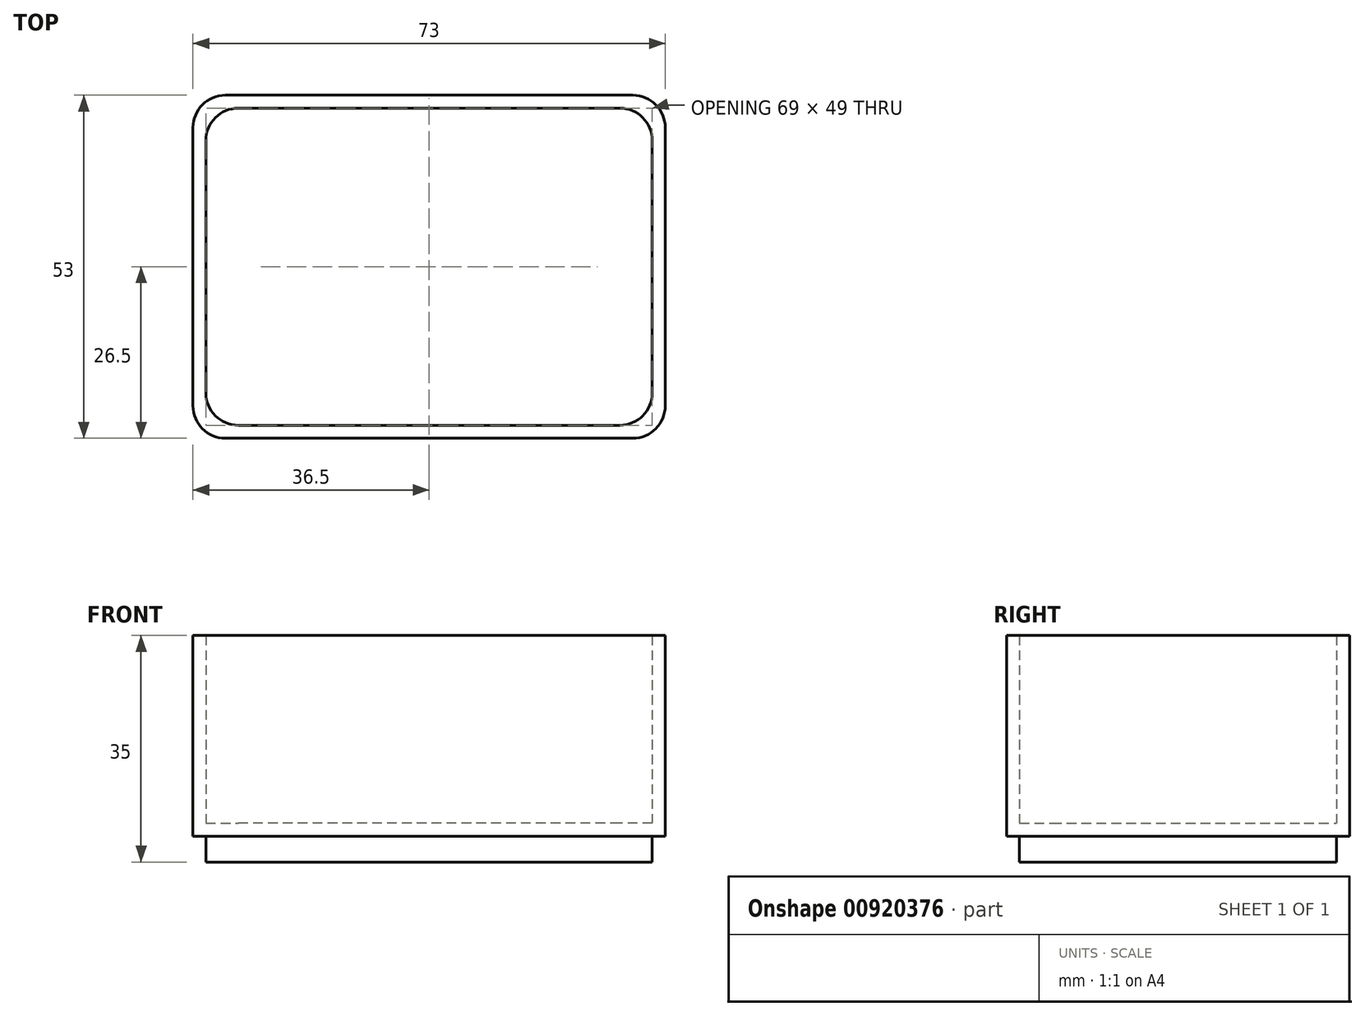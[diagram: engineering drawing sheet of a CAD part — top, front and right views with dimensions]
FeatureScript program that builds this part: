
annotation { "Feature Type Name" : "Feature", "Feature Type Description" : "" }
export const myFeature = defineFeature(function(context is Context, id is Id, definition is map)
    precondition{}
    {
        {
            var Q0;
            Q0=qCreatedBy(makeId("Top.planeOp"),FACE);
            var sketch = newSketch(context, id + "F0", { "sketchPlane" : qUnion([Q0])});
            skLineSegment(sketch, "E0.bottom", {"start": v(-29.5, 24.5) * mm, "end": v(29.5, 24.5) * mm});
            skLineSegment(sketch, "E0.top", {"start": v(-29.5, -24.5) * mm, "end": v(29.5, -24.5) * mm});
            skLineSegment(sketch, "E0.left", {"start": v(-34.5, 19.5) * mm, "end": v(-34.5, -19.5) * mm});
            skLineSegment(sketch, "E0.right", {"start": v(34.5, 19.5) * mm, "end": v(34.5, -19.5) * mm});
            skPoint(sketch, "E0.middle", {"position": v(0, 0) * mm});
            skLineSegment(sketch, "E1.bottom", {"start": v(-31.5, 26.5) * mm, "end": v(31.5, 26.5) * mm});
            skLineSegment(sketch, "E1.top", {"start": v(-31.5, -26.5) * mm, "end": v(31.5, -26.5) * mm});
            skLineSegment(sketch, "E1.left", {"start": v(-36.5, 21.5) * mm, "end": v(-36.5, -21.5) * mm});
            skLineSegment(sketch, "E1.right", {"start": v(36.5, 21.5) * mm, "end": v(36.5, -21.5) * mm});
            skPoint(sketch, "E2.visualSharp", {"position": v(-34.5, 24.5) * mm});
            skArc(sketch, "E2.filletArc", {"start": v(-29.5, 24.5) * mm, "mid": v(-33.04, 23.04) * mm, "end": v(-34.5, 19.5) * mm});
            skPoint(sketch, "E3.visualSharp", {"position": v(-36.5, 26.5) * mm});
            skArc(sketch, "E3.filletArc", {"start": v(-31.5, 26.5) * mm, "mid": v(-35.04, 25.04) * mm, "end": v(-36.5, 21.5) * mm});
            skPoint(sketch, "E4.visualSharp", {"position": v(36.5, 26.5) * mm});
            skArc(sketch, "E4.filletArc", {"start": v(36.5, 21.5) * mm, "mid": v(35.04, 25.04) * mm, "end": v(31.5, 26.5) * mm});
            skPoint(sketch, "E5.visualSharp", {"position": v(34.5, 24.5) * mm});
            skArc(sketch, "E5.filletArc", {"start": v(34.5, 19.5) * mm, "mid": v(33.04, 23.04) * mm, "end": v(29.5, 24.5) * mm});
            skPoint(sketch, "E6.visualSharp", {"position": v(34.5, -24.5) * mm});
            skArc(sketch, "E6.filletArc", {"start": v(29.5, -24.5) * mm, "mid": v(33.04, -23.04) * mm, "end": v(34.5, -19.5) * mm});
            skPoint(sketch, "E7.visualSharp", {"position": v(36.5, -26.5) * mm});
            skArc(sketch, "E7.filletArc", {"start": v(31.5, -26.5) * mm, "mid": v(35.04, -25.04) * mm, "end": v(36.5, -21.5) * mm});
            skPoint(sketch, "E8.visualSharp", {"position": v(-36.5, -26.5) * mm});
            skArc(sketch, "E8.filletArc", {"start": v(-36.5, -21.5) * mm, "mid": v(-35.04, -25.04) * mm, "end": v(-31.5, -26.5) * mm});
            skPoint(sketch, "E9.visualSharp", {"position": v(-34.5, -24.5) * mm});
            skArc(sketch, "E9.filletArc", {"start": v(-34.5, -19.5) * mm, "mid": v(-33.04, -23.04) * mm, "end": v(-29.5, -24.5) * mm});
            skSolve(sketch);
        }
        {
            var Q0;
            Q0=makeQuery(id+"F0.imprint","IMPRINT",FACE,{"disambiguationData":[TD([[makeQuery(id+"F0.imprint","IMPRINT",EDGE,{"derivedFrom":sQuery(id+"F0.wireOp",EDGE,"E0.bottom")}),-1.0]])]});
            var Q1;
            Q1=makeQuery(id+"F0.imprint","IMPRINT",FACE,{"disambiguationData":[TD([[makeQuery(id+"F0.imprint","IMPRINT",EDGE,{"derivedFrom":sQuery(id+"F0.wireOp",EDGE,"E0.bottom")}),1.0]])]});
            extrude(context, id + "F1", {"entities" : qUnion([Q0, Q1]), "depth" : 6 * mm, "offsetDistance" : 25 * mm});
        }
        {
            var Q0;
            Q0=makeQuery(id+"F0.imprint","IMPRINT",FACE,{"disambiguationData":[TD([[makeQuery(id+"F0.imprint","IMPRINT",EDGE,{"derivedFrom":sQuery(id+"F0.wireOp",EDGE,"E0.bottom")}),1.0]])]});
            extrude(context, id + "F2", {"entities" : qUnion([Q0]), "operationType" : NewBodyOperationType.ADD, "depth" : 35 * mm, "offsetDistance" : 25 * mm});
        }
        {
            var Q0;
            Q0=makeQuery(id+"F0.imprint","IMPRINT",FACE,{"disambiguationData":[TD([[makeQuery(id+"F0.imprint","IMPRINT",EDGE,{"derivedFrom":sQuery(id+"F0.wireOp",EDGE,"E0.bottom")}),1.0]])]});
            extrude(context, id + "F3", {"entities" : qUnion([Q0]), "operationType" : NewBodyOperationType.REMOVE, "oppositeDirection" : true, "depth" : -4 * mm, "offsetDistance" : 25 * mm});
        }
    });
